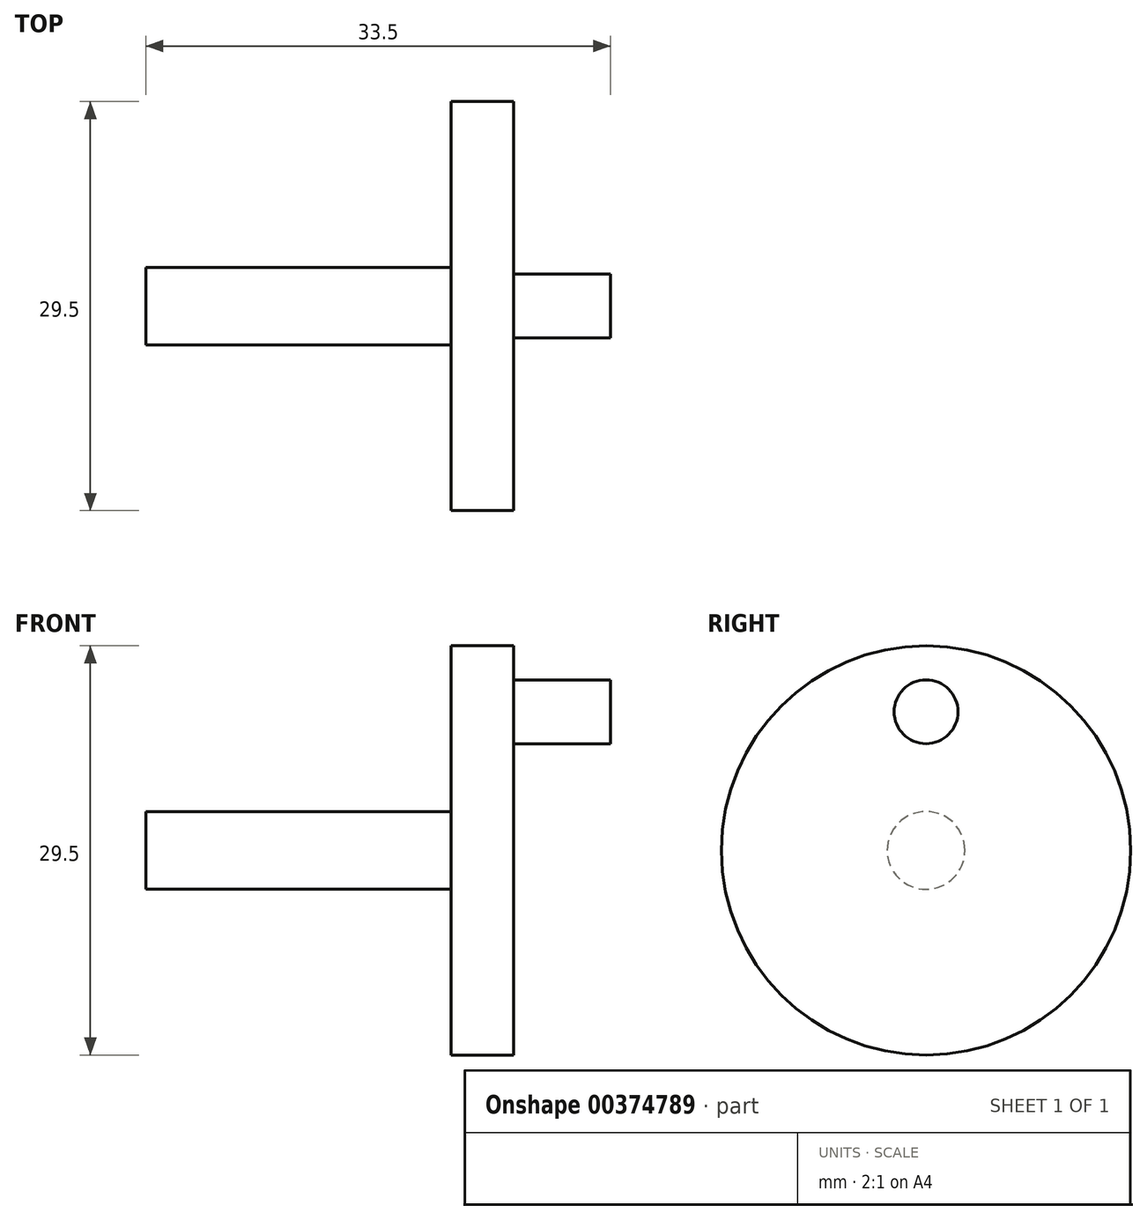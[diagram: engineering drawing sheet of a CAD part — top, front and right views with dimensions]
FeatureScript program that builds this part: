
annotation { "Feature Type Name" : "Feature", "Feature Type Description" : "" }
export const myFeature = defineFeature(function(context is Context, id is Id, definition is map)
    precondition{}
    {
        {
            var Q0;
            Q0=qCreatedBy(makeId("Right.planeOp"),FACE);
            var sketch = newSketch(context, id + "F0", { "sketchPlane" : qUnion([Q0])});
            skCircle(sketch, "E0", {"center": v(0, 0) * mm, "radius": 14.75 * mm});
            skSolve(sketch);
        }
        {
            var Q0;
            Q0 = qSketchRegion(id + "F0", true);
            extrude(context, id + "F1", {"entities" : qUnion([Q0]), "depth" : 4.5 * mm});
        }
        {
            var Q0;
            Q0=makeQuery(id+"F1.opExtrude","CAP_FACE",FACE,{"disambiguationData":[OSD([sQuery(id+"F0.wireOp",EDGE,"E0")])],"isStart":true});
            var sketch = newSketch(context, id + "F2", { "sketchPlane" : qUnion([Q0])});
            skCircle(sketch, "E1", {"center": v(0, 0) * mm, "radius": 2.8 * mm});
            skSolve(sketch);
        }
        {
            var Q0;
            Q0 = qSketchRegion(id + "F2", true);
            extrude(context, id + "F3", {"entities" : qUnion([Q0]), "operationType" : NewBodyOperationType.ADD, "depth" : 17 * mm});
        }
        {
            var Q0;
            Q0=makeQuery(id+"F1.opExtrude","CAP_FACE",FACE,{"disambiguationData":[OSD([sQuery(id+"F0.wireOp",EDGE,"E0")])],"isStart":false});
            var sketch = newSketch(context, id + "F4", { "sketchPlane" : qUnion([Q0])});
            skLineSegment(sketch, "E2", {"start": v(0, 14.75) * mm, "end": v(0, -14.75) * mm, "construction": true});
            skPoint(sketch, "E3", {"position": v(0, 10) * mm});
            skCircle(sketch, "E4", {"center": v(0, 10) * mm, "radius": 2.3 * mm});
            skSolve(sketch);
        }
        {
            var Q0;
            Q0 = qSketchRegion(id + "F4", true);
            extrude(context, id + "F5", {"entities" : qUnion([Q0]), "operationType" : NewBodyOperationType.ADD, "depth" : 7 * mm});
        }
        {
            var Q0;
            Q0=makeQuery(id+"F3.opExtrude","CAP_FACE",FACE,{"disambiguationData":[OSD([sQuery(id+"F2.wireOp",EDGE,"E1")])],"isStart":false});
            extrude(context, id + "F6", {"entities" : qUnion([Q0]), "operationType" : NewBodyOperationType.ADD, "depth" : 5 * mm, "offsetDistance" : 25 * mm});
        }
    });
